# Revit family: Mini MP 160 V.V. (a)
name_source: partatom
category: Equipement spécialisé
revit_build: Autodesk Revit LT 2015 (Build: 20140606_1530(x64)
units: mm (PartAtom-declared; Revit-internal decimal feet)

## types (5) — shared parameters
Apparent Power = 0 VA
Depth = 78 mm  [stored 0.255906 ft]
Depth Electrique connexion = 39 mm  [stored 0.127953 ft]
Description = MIXERS PLONGEANTS GAMME MINI
Fabricant = ROBOT COUPE
Height = 450 mm  [stored 1.47638 ft]
Height Electrique connexion = 440 mm  [stored 1.44357 ft]
Modèle = Mini MP 160 V.V.
Phase = 1
URL = www.robot-coupe.com
Width = 115 mm  [stored 0.377297 ft]
water = Connector
zero-valued in all types: Cold water supply, Cold water supply height, Used water, Waste water height

## per-type parameters (varying)
| type | Amps | Cycle | Speeds (Rpm) | Volts | Watts | Weight |
| Mini MP 160 V.V.   230/50/1 | 1.1 A | 50 Hz | 2000 to 12500 | 230 V | 220 W | 2.4 kg |
| Mini MP 160 V.V.   240/50/1 | 1.1 A | 50 Hz | 2000 to 12500 | 240 V | 220 W | 2.4 kg |
| Mini MP 160 V.V.   120/60/1 | 1.9 A | 60 Hz | 2000 to 12500 | 120 V | 220 W | 2.4 kg |
| Mini MP 160 V.V.   220/60/1 | 1.1 A | 60 Hz | 2000 to 12500 | 220 V | 220 W | 2.4 kg |
| Mini MP 160 V.V. USA   120/60/1 | 1.8 A | 60 Hz | 2,000 to 12,500 | 120 V | 240 W | 5 lbs |

note: [stored X ft] marks values corroborated as IEEE doubles in the binary element streams (Revit-internal decimal feet)

## geometry (parser evidence)
native form markers: Blend x106, Sweep x4
no freeform markers — native parametric forms only
